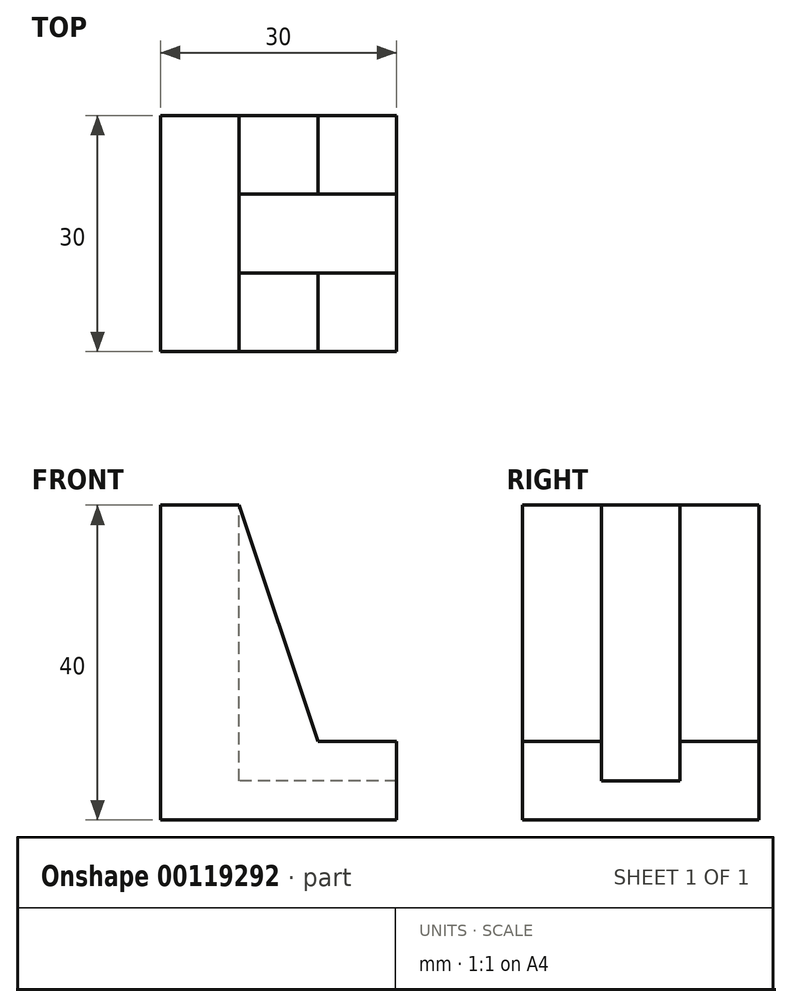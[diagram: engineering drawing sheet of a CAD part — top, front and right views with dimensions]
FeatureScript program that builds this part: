
annotation { "Feature Type Name" : "Feature", "Feature Type Description" : "" }
export const myFeature = defineFeature(function(context is Context, id is Id, definition is map)
    precondition{}
    {
        {
            var Q0;
            Q0=qCreatedBy(makeId("Front.planeOp"),FACE);
            var sketch = newSketch(context, id + "F0", { "sketchPlane" : qUnion([Q0])});
            skLineSegment(sketch, "E0", {"start": v(0, 40) * mm, "end": v(10, 40) * mm});
            skLineSegment(sketch, "E1", {"start": v(20, 10) * mm, "end": v(10, 40) * mm});
            skLineSegment(sketch, "E2", {"start": v(20, 10) * mm, "end": v(30, 10) * mm});
            skLineSegment(sketch, "E3", {"start": v(30, 10) * mm, "end": v(30, 0) * mm});
            skLineSegment(sketch, "E4", {"start": v(30, 0) * mm, "end": v(0, 0) * mm});
            skLineSegment(sketch, "E5", {"start": v(0, 0) * mm, "end": v(0, 40) * mm});
            skLineSegment(sketch, "E6", {"start": v(30, 0) * mm, "end": v(30, 10) * mm});
            skSolve(sketch);
        }
        {
            var Q0;
            Q0=makeQuery(id+"F0.imprint","IMPRINT",FACE,{"disambiguationData":[TD([[makeQuery(id+"F0.imprint","IMPRINT",EDGE,{"derivedFrom":sQuery(id+"F0.wireOp",EDGE,"E0")}),-1.0]])]});
            extrude(context, id + "F1", {"entities" : qUnion([Q0]), "depth" : 30 * mm});
        }
        {
            var Q0;
            Q0=makeQuery(id+"F1.opExtrude","SWEPT_FACE",FACE,{"disambiguationData":[OSD([sQuery(id+"F0.wireOp",EDGE,"E0")])]});
            var sketch = newSketch(context, id + "F2", { "sketchPlane" : qUnion([Q0])});
            skLineSegment(sketch, "E7.bottom", {"start": v(35.91, -10) * mm, "end": v(10, -10) * mm});
            skLineSegment(sketch, "E7.top", {"start": v(35.91, -20) * mm, "end": v(10, -20) * mm});
            skLineSegment(sketch, "E7.left", {"start": v(35.91, -10) * mm, "end": v(35.91, -20) * mm});
            skLineSegment(sketch, "E7.right", {"start": v(10, -10) * mm, "end": v(10, -20) * mm});
            skSolve(sketch);
        }
        {
            var Q0;
            Q0 = qSketchRegion(id + "F2", true);
            extrude(context, id + "F3", {"entities" : qUnion([Q0]), "operationType" : NewBodyOperationType.REMOVE, "oppositeDirection" : true, "depth" : 35 * mm});
        }
    });
